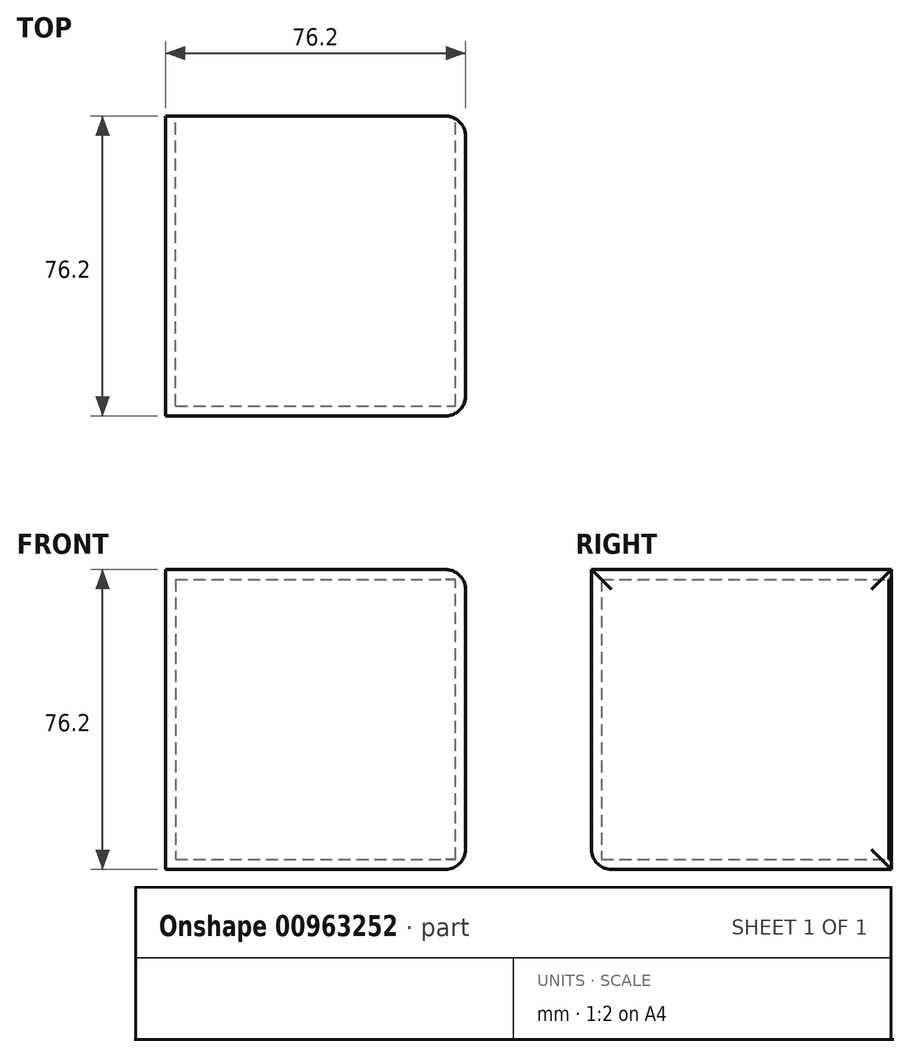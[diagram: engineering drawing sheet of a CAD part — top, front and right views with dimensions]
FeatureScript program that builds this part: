
annotation { "Feature Type Name" : "Feature", "Feature Type Description" : "" }
export const myFeature = defineFeature(function(context is Context, id is Id, definition is map)
    precondition{}
    {
        {
            var Q0;
            Q0=qCreatedBy(makeId("Front.planeOp"),FACE);
            var sketch = newSketch(context, id + "F0", { "sketchPlane" : qUnion([Q0])});
            skLineSegment(sketch, "E0.bottom", {"start": v(-39.35, 31.96) * mm, "end": v(36.85, 31.96) * mm});
            skLineSegment(sketch, "E0.top", {"start": v(-39.35, -44.24) * mm, "end": v(36.85, -44.24) * mm});
            skLineSegment(sketch, "E0.left", {"start": v(-39.35, 31.96) * mm, "end": v(-39.35, -44.24) * mm});
            skLineSegment(sketch, "E0.right", {"start": v(36.85, 31.96) * mm, "end": v(36.85, -44.24) * mm});
            skSolve(sketch);
        }
        {
            var Q0;
            Q0=makeQuery(id+"F0.imprint","IMPRINT",FACE,{"disambiguationData":[TD([[makeQuery(id+"F0.imprint","IMPRINT",EDGE,{"derivedFrom":sQuery(id+"F0.wireOp",EDGE,"E0.bottom")}),-1.0]])]});
            extrude(context, id + "F1", {"entities" : qUnion([Q0]), "depth" : 76.2 * mm, "offsetDistance" : 25.4 * mm});
        }
        {
            var Q0;
            Q0=makeQuery(id+"F1.opExtrude","CAP_FACE",FACE,{"disambiguationData":[OSD([sQuery(id+"F0.wireOp",EDGE,"E0.bottom"),sQuery(id+"F0.wireOp",EDGE,"E0.top"),sQuery(id+"F0.wireOp",EDGE,"E0.left"),sQuery(id+"F0.wireOp",EDGE,"E0.right")])],"isStart":true});
            shell(context, id + "F2", {"entities" : qUnion([Q0]), "thickness" : 2.54 * mm});
        }
        {
            var Q0;
            Q0=makeQuery(id+"F1.opExtrude","CAP_EDGE",EDGE,{"disambiguationData":[OSD([sQuery(id+"F0.wireOp",EDGE,"E0.right")])],"isStart":false});
            var Q1;
            Q1=makeQuery(id+"F1.opExtrude","CAP_EDGE",EDGE,{"disambiguationData":[OSD([sQuery(id+"F0.wireOp",EDGE,"E0.top")])],"isStart":false});
            var Q2;
            Q2=makeQuery(id+"F1.opExtrude","SWEPT_EDGE",EDGE,{"disambiguationData":[OSD([sQuery(id+"F0.wireOp",EDGE,"E0.top"),sQuery(id+"F0.wireOp",EDGE,"E0.right")])]});
            var Q3;
            Q3=makeQuery(id+"F1.opExtrude","CAP_EDGE",EDGE,{"disambiguationData":[OSD([sQuery(id+"F0.wireOp",EDGE,"E0.right")])],"isStart":true});
            var Q4;
            Q4=makeQuery(id+"F1.opExtrude","SWEPT_EDGE",EDGE,{"disambiguationData":[OSD([sQuery(id+"F0.wireOp",EDGE,"E0.bottom"),sQuery(id+"F0.wireOp",EDGE,"E0.right")])]});
            fillet(context, id + "F3", {"entities" : qUnion([Q0, Q1, Q2, Q3, Q4]), "radius" : 5.08 * mm, "tangentPropagation" : true, "allowEdgeOverflow" : false});
        }
    });
